# Revit family: PRD_FrankeWS_WlHngWshBsns_WashinoChildrenWashTrough_SANW212
name_source: partatom
category: Plumbing Fixtures
revit_build: Autodesk Revit 2018 (Build: 20190510_1515(x64)
units: mm (PartAtom-declared; Revit-internal decimal feet)

## family parameters
Cut with Voids When Loaded = No
Host = Face
OmniClass Number = 23.45.05.14.14
OmniClass Title = Sinks/Lavatories
Part Type = Normal
Room Calculation Point = No
Round Connector Dimension = Use Diameter
Shared = No

## types (1)
- SANW212
    AssetType = Fixed
    BIMObjectName = PRD_AR_WallHungWashBasins_WashinoChildrenWashTrough_SANW212
    Category = Pr_40_20_96_96, Wall-hung wash basins
    Color = Alpinewhite
    Default Elevation = 850 mm  [stored 2.78871 ft]
    Description = WASHINO Children's Wash-and-Play Trough made of MIRANIT resin-bonded mineral material, with a smooth, pore-free surface (temperature-resistant up to 80°C). Alpine white colour. With 4 wash places (2 wash places with a height difference of 100 mm), wave-shaped basins with reduced extension to increase accessibility to the tap, large outer radii of basins to minimise risk of injury, large inner radii facilitate easy cleaning. Tap landing with a tap hole for each wash place. Integrated divider with overflow function made of MIRANIT, blue colour (RAL 5002).Waste and overflow valve DN 40 x 120 mm implemented as a standpipe for 2 wash places. Integral back panel for fixing. Mounting material included. Version with basin right above/left below
    DividerMaterial = PRD_AR_Miranit_RAL5002
    DrainSize = DN 40 (1 1/2 inch)
    DurationUnit = year
    Features = mineral material, wall mounting, 2100x240x470 mm (WxHxD)
    Form = Wall hung wash basin
    GrossWeight = 95.00 kg
    IfcExportAs = IfcSanitaryTerminalType
    IfcExportType = WASHHANDBASIN
    IntegralAccessories = Mounting material included.
    Manufacturer = KWC Group AG
    ManufacturerName = KWC Group AG
    ManufacturerURL = www.kwc.com
    Material = Mineral material
    MaterialsBody = Miranit
    MaterialsFinishAndColour = Alpinewhite
    Model = SANW212
    ModelNumber = 2000103059
    ModelReference = SANW212
    NBSDescription = Wall hung wash basins
    NBSReference = 45-35-70/369
    Name = WASHINO Children's Wash-and-Play Trough SANW212
    NetWeight = 90.50 kg
    NominalDepth = 470 mm  [stored 1.54199 ft]
    NominalHeight = 240 mm  [stored 0.787402 ft]
    NominalLength = 240 mm  [stored 0.787402 ft]
    NominalWidth = 2100 mm
    ProductInformation = https://pim.kwc.com
    Size = 2100 x 240 x 470
    URL = www.kwc.com
    Uniclass2015Code = Pr_40_20_96_96
    Uniclass2015Title = Wall-hung wash basins
    Uniclass2015Version = Products v1.7
    Version = 1
    WarrantyDurationUnit = year
    WashHandBasinMounting = WallHung
    WashHandBasinType = Other
    WashbasinMaterial = PRD_AR_Miranit_Alpinewhite
    WasteSize = 40  [stored 0.131234 ft]
    WasteValveMaterial = PRD_AR_StainlessSteel_SatinFinished
    WaterSupplyOverflowAndWasteHolesOverflow = None
    WaterSupplyOverflowAndWasteHolesWaste = Center-Center
    WaterSupplyOverflowAndWasteHolesWaterSupply = 4 tap holes

note: [stored X ft] marks values corroborated as IEEE doubles in the binary element streams (Revit-internal decimal feet)

## geometry (parser evidence)
native form markers: Sweep x5
no freeform markers — native parametric forms only
